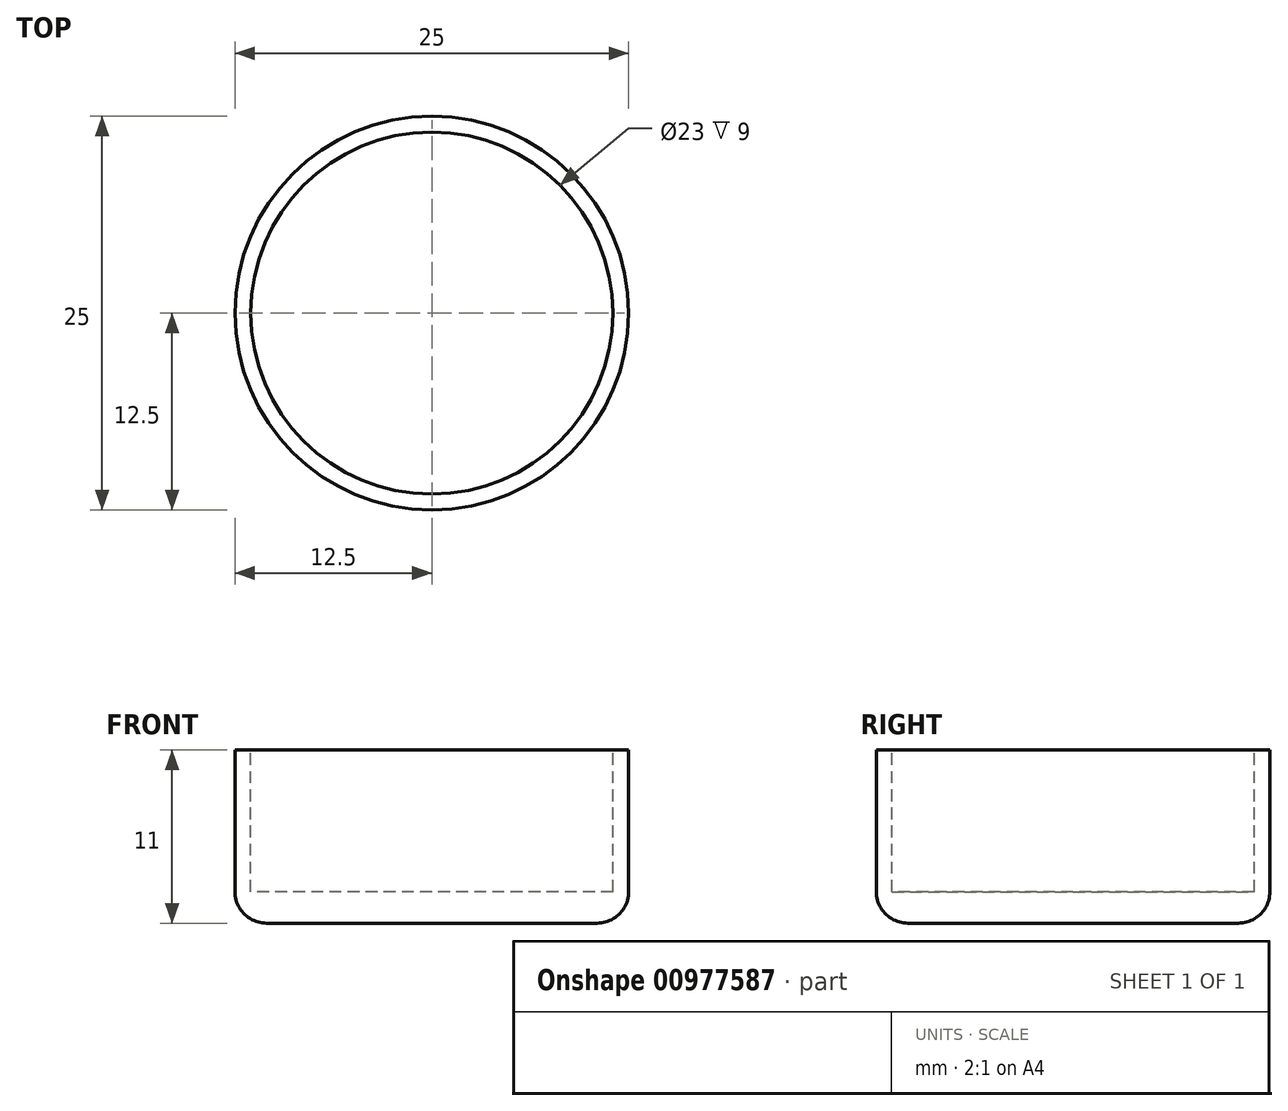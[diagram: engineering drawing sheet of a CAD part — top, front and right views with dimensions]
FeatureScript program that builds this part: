
annotation { "Feature Type Name" : "Feature", "Feature Type Description" : "" }
export const myFeature = defineFeature(function(context is Context, id is Id, definition is map)
    precondition{}
    {
        {
            var Q0;
            Q0=qCreatedBy(makeId("Top.planeOp"),FACE);
            var sketch = newSketch(context, id + "F0", { "sketchPlane" : qUnion([Q0])});
            skCircle(sketch, "E0", {"center": v(0, 0) * mm, "radius": 12.5 * mm});
            skSolve(sketch);
        }
        {
            var Q0;
            Q0 = qSketchRegion(id + "F0", true);
            extrude(context, id + "F1", {"entities" : qUnion([Q0]), "depth" : 11 * mm, "offsetDistance" : 25 * mm});
        }
        {
            var Q0;
            Q0=makeQuery(id+"F1.opExtrude","CAP_FACE",FACE,{"disambiguationData":[OSD([sQuery(id+"F0.wireOp",EDGE,"E0")])],"isStart":false});
            var sketch = newSketch(context, id + "F2", { "sketchPlane" : qUnion([Q0])});
            skCircle(sketch, "E1", {"center": v(0, 0) * mm, "radius": 11.5 * mm});
            skSolve(sketch);
        }
        {
            var Q0;
            Q0 = qSketchRegion(id + "F2", true);
            extrude(context, id + "F3", {"entities" : qUnion([Q0]), "operationType" : NewBodyOperationType.REMOVE, "oppositeDirection" : true, "depth" : 9 * mm, "offsetDistance" : 25 * mm});
        }
        {
            var Q0;
            Q0=makeQuery(id+"F1.opExtrude","CAP_EDGE",EDGE,{"disambiguationData":[OSD([sQuery(id+"F0.wireOp",EDGE,"E0")])],"isStart":true});
            fillet(context, id + "F4", {"entities" : qUnion([Q0]), "radius" : 2 * mm, "tangentPropagation" : true, "allowEdgeOverflow" : false});
        }
    });
